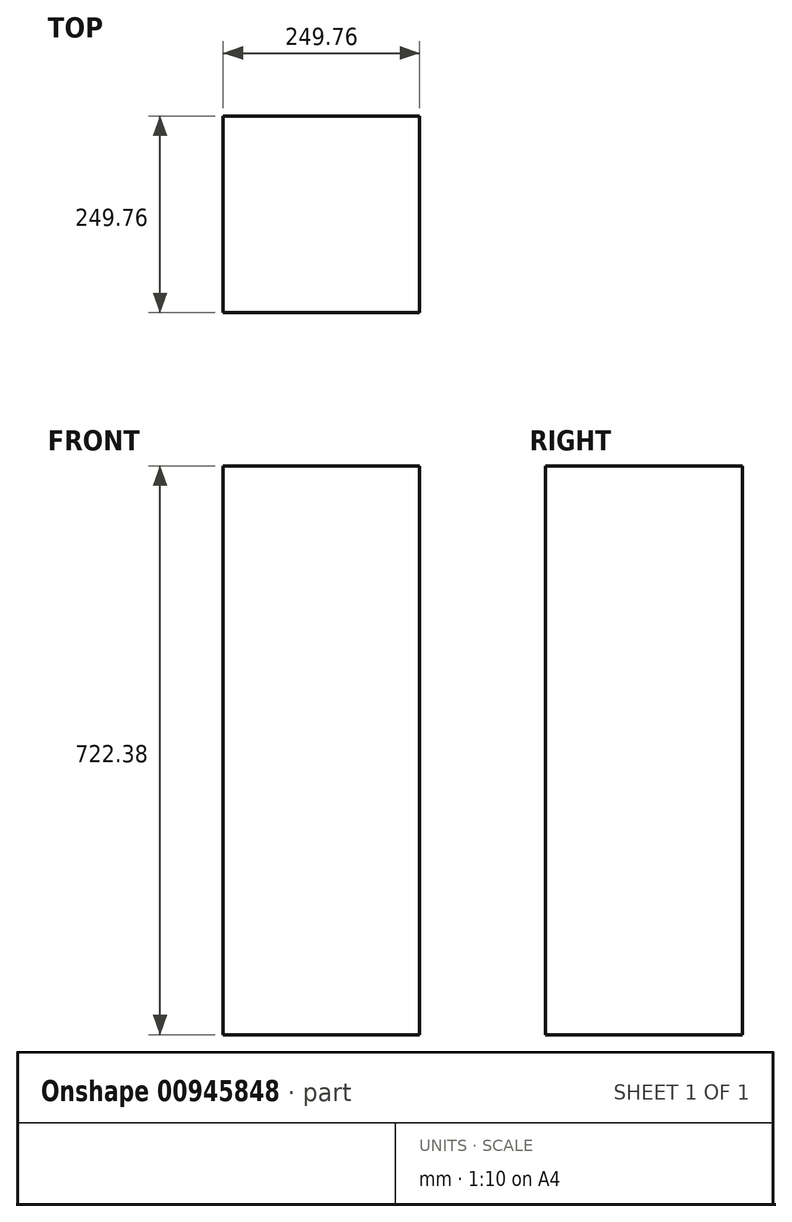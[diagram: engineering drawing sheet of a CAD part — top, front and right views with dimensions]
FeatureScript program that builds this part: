
annotation { "Feature Type Name" : "Feature", "Feature Type Description" : "" }
export const myFeature = defineFeature(function(context is Context, id is Id, definition is map)
    precondition{}
    {
        {
            var Q0;
            Q0=qCreatedBy(makeId("Top.planeOp"),FACE);
            var sketch = newSketch(context, id + "F0", { "sketchPlane" : qUnion([Q0])});
            skLineSegment(sketch, "E0.bottom", {"start": v(-249.76, 249.76) * mm, "end": v(0, 249.76) * mm});
            skLineSegment(sketch, "E0.top", {"start": v(-249.76, 0) * mm, "end": v(0, 0) * mm});
            skLineSegment(sketch, "E0.left", {"start": v(-249.76, 249.76) * mm, "end": v(-249.76, 0) * mm});
            skLineSegment(sketch, "E0.right", {"start": v(0, 249.76) * mm, "end": v(0, 0) * mm});
            skSolve(sketch);
        }
        {
            var Q0;
            Q0=makeQuery(id+"F0.imprint","IMPRINT",FACE,{"disambiguationData":[TD([[makeQuery(id+"F0.imprint","IMPRINT",EDGE,{"derivedFrom":sQuery(id+"F0.wireOp",EDGE,"E0.bottom")}),-1.0]])]});
            extrude(context, id + "F1", {"entities" : qUnion([Q0]), "depth" : 722.38 * mm, "offsetDistance" : 25.4 * mm});
        }
    });
